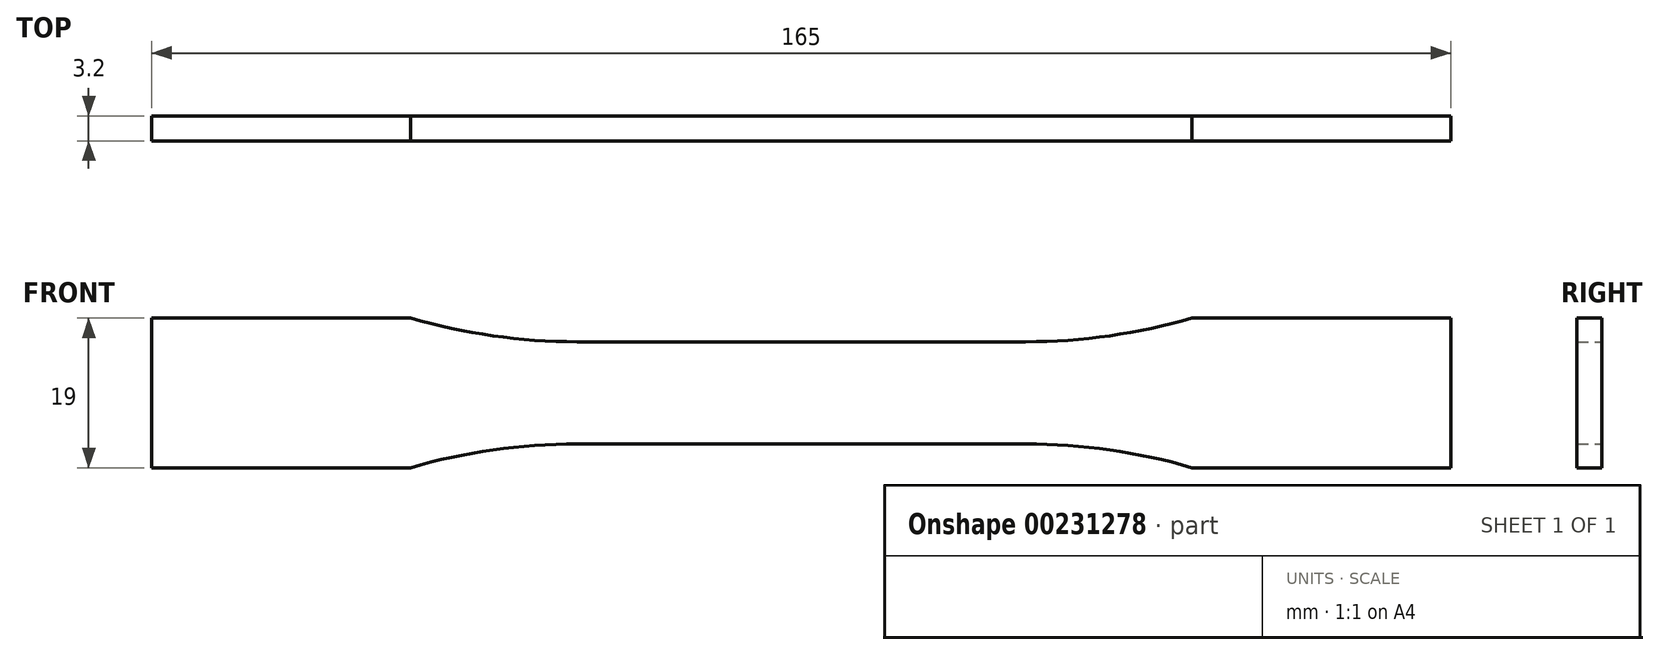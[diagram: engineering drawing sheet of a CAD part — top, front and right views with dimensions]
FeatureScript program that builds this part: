
annotation { "Feature Type Name" : "Feature", "Feature Type Description" : "" }
export const myFeature = defineFeature(function(context is Context, id is Id, definition is map)
    precondition{}
    {
        {
            var Q0;
            Q0=qCreatedBy(makeId("Front.planeOp"),FACE);
            var sketch = newSketch(context, id + "F0", { "sketchPlane" : qUnion([Q0])});
            skLineSegment(sketch, "E0.bottom", {"start": v(82.5, 9.5) * mm, "end": v(49.64, 9.5) * mm});
            skLineSegment(sketch, "E0.top", {"start": v(82.5, -9.5) * mm, "end": v(49.64, -9.5) * mm});
            skLineSegment(sketch, "E0.left", {"start": v(82.5, 9.5) * mm, "end": v(82.5, -9.5) * mm});
            skLineSegment(sketch, "E0.right", {"start": v(-82.5, 9.5) * mm, "end": v(-82.5, -9.5) * mm});
            skPoint(sketch, "E0.middle", {"position": v(0, 0) * mm});
            skLineSegment(sketch, "E1.bottom", {"start": v(28.5, -6.5) * mm, "end": v(-28.5, -6.5) * mm});
            skLineSegment(sketch, "E1.top", {"start": v(28.5, 6.5) * mm, "end": v(-28.5, 6.5) * mm});
            skArc(sketch, "E2", {"start": v(-49.64, 9.5) * mm, "mid": v(-39.18, 7.25) * mm, "end": v(-28.5, 6.5) * mm});
            skLineSegment(sketch, "E3", {"start": v(28.5, 6.5) * mm, "end": v(28.5, 9.5) * mm});
            skPoint(sketch, "E3.endSnap0", {"position": v(28.5, 0) * mm});
            skArc(sketch, "E4", {"start": v(28.5, 6.5) * mm, "mid": v(39.18, 7.25) * mm, "end": v(49.64, 9.5) * mm});
            skArc(sketch, "E5", {"start": v(-28.5, -6.5) * mm, "mid": v(-39.18, -7.25) * mm, "end": v(-49.64, -9.5) * mm});
            skArc(sketch, "E6", {"start": v(49.64, -9.5) * mm, "mid": v(39.18, -7.25) * mm, "end": v(28.5, -6.5) * mm});
            skLineSegment(sketch, "E7.trimOffspring", {"start": v(-49.64, 9.5) * mm, "end": v(-82.5, 9.5) * mm});
            skLineSegment(sketch, "E8.trimOffspring", {"start": v(-49.64, -9.5) * mm, "end": v(-82.5, -9.5) * mm});
            skSolve(sketch);
        }
        {
            var Q0;
            Q0 = qSketchRegion(id + "F0", true);
            extrude(context, id + "F1", {"entities" : qUnion([Q0]), "depth" : 3.2 * mm});
        }
    });
